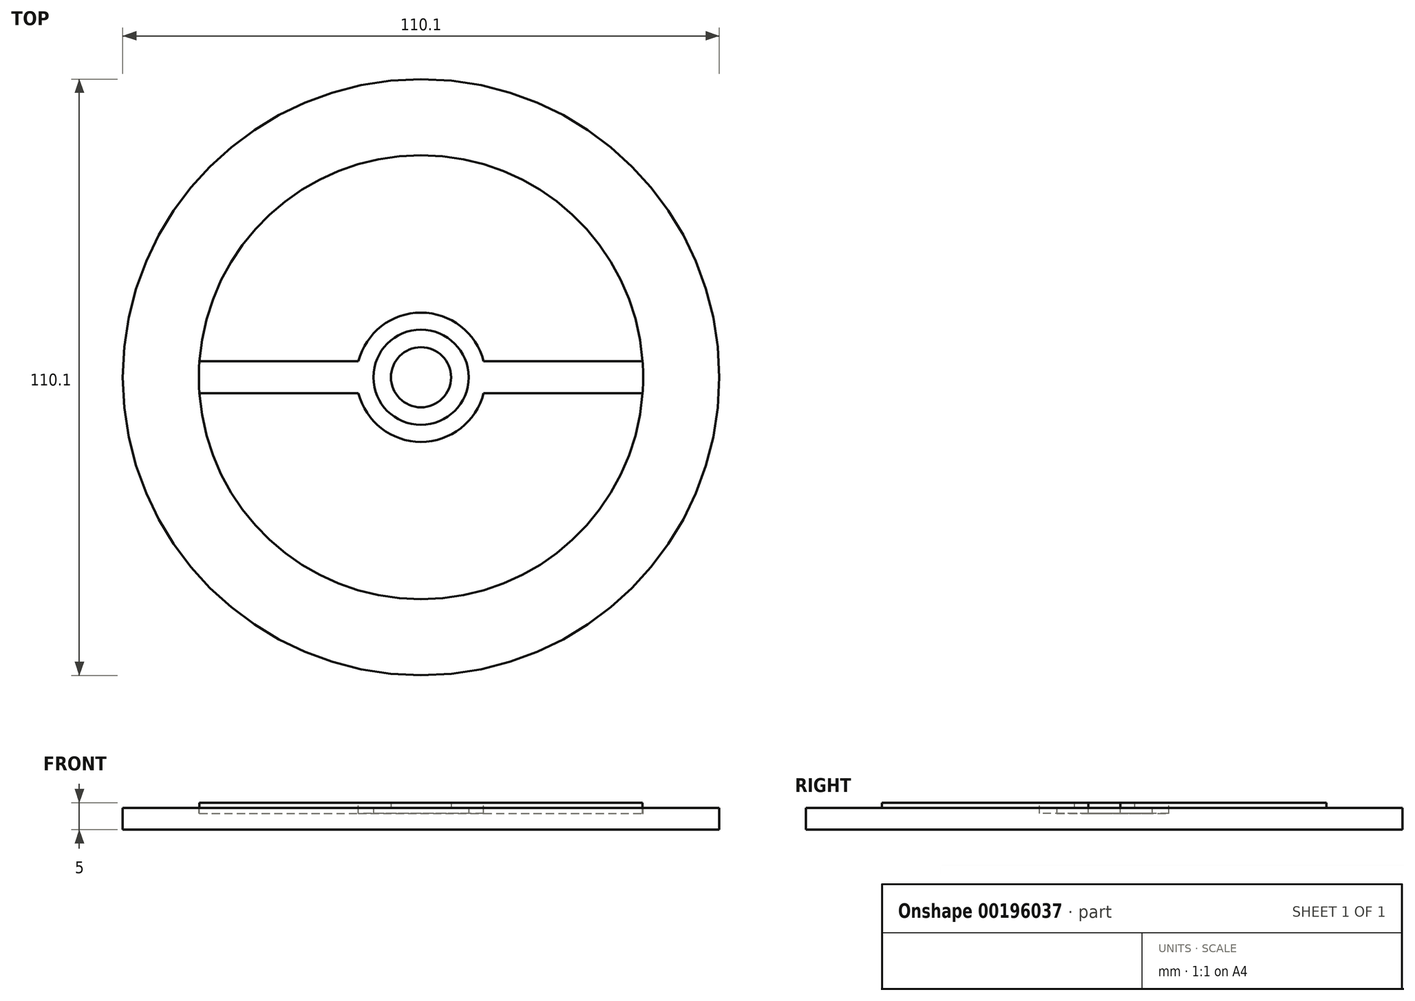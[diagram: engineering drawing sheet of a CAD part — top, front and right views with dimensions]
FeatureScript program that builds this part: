
annotation { "Feature Type Name" : "Feature", "Feature Type Description" : "" }
export const myFeature = defineFeature(function(context is Context, id is Id, definition is map)
    precondition{}
    {
        {
            var Q0;
            Q0=qCreatedBy(makeId("Top.planeOp"),FACE);
            var sketch = newSketch(context, id + "F0", { "sketchPlane" : qUnion([Q0])});
            skCircle(sketch, "E0", {"center": v(0, 0) * mm, "radius": 55.05 * mm});
            skSolve(sketch);
        }
        {
            var Q0;
            Q0=makeQuery(id+"F0.imprint","IMPRINT",FACE,{"disambiguationData":[TD([[makeQuery(id+"F0.imprint","IMPRINT",EDGE,{"derivedFrom":sQuery(id+"F0.wireOp",EDGE,"E0")}),1.0]])]});
            extrude(context, id + "F1", {"entities" : qUnion([Q0]), "depth" : 4 * mm});
        }
        {
            var Q0;
            Q0=makeQuery(id+"F1.opExtrude","CAP_FACE",FACE,{"disambiguationData":[OSD([sQuery(id+"F0.wireOp",EDGE,"E0")])],"isStart":false});
            var sketch = newSketch(context, id + "F2", { "sketchPlane" : qUnion([Q0])});
            skCircle(sketch, "E1", {"center": v(0, 0) * mm, "radius": 41 * mm});
            skSolve(sketch);
        }
        {
            var Q0;
            Q0=makeQuery(id+"F2.imprint","IMPRINT",FACE,{"disambiguationData":[TD([[makeQuery(id+"F2.imprint","IMPRINT",EDGE,{"derivedFrom":sQuery(id+"F2.wireOp",EDGE,"E1")}),1.0]])]});
            extrude(context, id + "F3", {"entities" : qUnion([Q0]), "operationType" : NewBodyOperationType.ADD, "depth" : 1 * mm});
        }
        {
            var Q0;
            Q0=makeQuery(id+"F3.opExtrude","CAP_FACE",FACE,{"disambiguationData":[OSD([sQuery(id+"F2.wireOp",EDGE,"E1")])],"isStart":false});
            var sketch = newSketch(context, id + "F4", { "sketchPlane" : qUnion([Q0])});
            skCircle(sketch, "E2", {"center": v(0, 0) * mm, "radius": 11.93 * mm});
            skSolve(sketch);
        }
        {
            var Q0;
            Q0=makeQuery(id+"F4.imprint","IMPRINT",FACE,{"disambiguationData":[TD([[makeQuery(id+"F4.imprint","IMPRINT",EDGE,{"derivedFrom":sQuery(id+"F4.wireOp",EDGE,"E2")}),1.0]])]});
            extrude(context, id + "F5", {"entities" : qUnion([Q0]), "operationType" : NewBodyOperationType.REMOVE, "oppositeDirection" : true, "depth" : 2 * mm});
        }
        {
            var Q0;
            Q0=makeQuery(id+"F5.boolean.opBoolean","COPY",FACE,{"derivedFrom":makeQuery(id+"F5.opExtrude","CAP_FACE",FACE,{"disambiguationData":[OSD([sQuery(id+"F4.wireOp",EDGE,"E2")])],"isStart":false})});
            var sketch = newSketch(context, id + "F6", { "sketchPlane" : qUnion([Q0])});
            skCircle(sketch, "E3", {"center": v(0, 0) * mm, "radius": 8.8 * mm});
            skSolve(sketch);
        }
        {
            var Q0;
            Q0=makeQuery(id+"F6.imprint","IMPRINT",FACE,{"disambiguationData":[TD([[makeQuery(id+"F6.imprint","IMPRINT",EDGE,{"derivedFrom":sQuery(id+"F6.wireOp",EDGE,"E3")}),1.0]])]});
            extrude(context, id + "F7", {"entities" : qUnion([Q0]), "operationType" : NewBodyOperationType.ADD, "depth" : 1 * mm});
        }
        {
            var Q0;
            Q0=makeQuery(id+"F7.opExtrude","CAP_FACE",FACE,{"disambiguationData":[OSD([sQuery(id+"F6.wireOp",EDGE,"E3")])],"isStart":false});
            var sketch = newSketch(context, id + "F8", { "sketchPlane" : qUnion([Q0])});
            skCircle(sketch, "E4", {"center": v(0, 0) * mm, "radius": 5.55 * mm});
            skSolve(sketch);
        }
        {
            var Q0;
            Q0 = qSketchRegion(id + "F8", true);
            extrude(context, id + "F9", {"entities" : qUnion([Q0]), "operationType" : NewBodyOperationType.ADD, "depth" : 1 * mm});
        }
        {
            var Q0;
            Q0=makeQuery(id+"F3.opExtrude","CAP_FACE",FACE,{"disambiguationData":[OSD([sQuery(id+"F2.wireOp",EDGE,"E1")])],"isStart":false});
            var sketch = newSketch(context, id + "F10", { "sketchPlane" : qUnion([Q0])});
            skLineSegment(sketch, "E5", {"start": v(-40.9, 2.94) * mm, "end": v(-11.56, 2.94) * mm});
            skLineSegment(sketch, "E6", {"start": v(-11.56, -2.94) * mm, "end": v(-40.9, -2.94) * mm});
            skSolve(sketch);
        }
        {
            var Q0;
            Q0 = qSketchRegion(id + "F10", true);
            var Q1;
            {var subQ0=sQuery(id+"F10.wireOp",EDGE,"E5");Q1=makeQuery(id+"F10.imprint","IMPRINT",FACE,{"disambiguationData":[TD([[makeQuery(id+"F10.imprint","IMPRINT",EDGE,{"derivedFrom":subQ0}),-1.0]])]});}
            extrude(context, id + "F11", {"entities" : qUnion([Q0, Q1]), "operationType" : NewBodyOperationType.REMOVE, "oppositeDirection" : true, "depth" : 2 * mm});
        }
        {
            var Q0;
            Q0=makeQuery(id+"F3.opExtrude","CAP_FACE",FACE,{"disambiguationData":[OSD([sQuery(id+"F2.wireOp",EDGE,"E1")])],"isStart":false});
            var sketch = newSketch(context, id + "F12", { "sketchPlane" : qUnion([Q0])});
            skLineSegment(sketch, "E7", {"start": v(11.56, 2.96) * mm, "end": v(40.9, 2.96) * mm});
            skLineSegment(sketch, "E8", {"start": v(11.56, -2.94) * mm, "end": v(40.9, -2.94) * mm});
            skSolve(sketch);
        }
        {
            var Q0;
            Q0 = qSketchRegion(id + "F12", true);
            var Q1;
            {var subQ0=sQuery(id+"F12.wireOp",EDGE,"E7");Q1=makeQuery(id+"F12.imprint","IMPRINT",FACE,{"disambiguationData":[TD([[makeQuery(id+"F12.imprint","IMPRINT",EDGE,{"derivedFrom":subQ0}),-1.0]])]});}
            extrude(context, id + "F13", {"entities" : qUnion([Q0, Q1]), "operationType" : NewBodyOperationType.REMOVE, "oppositeDirection" : true, "depth" : 2 * mm});
        }
    });
